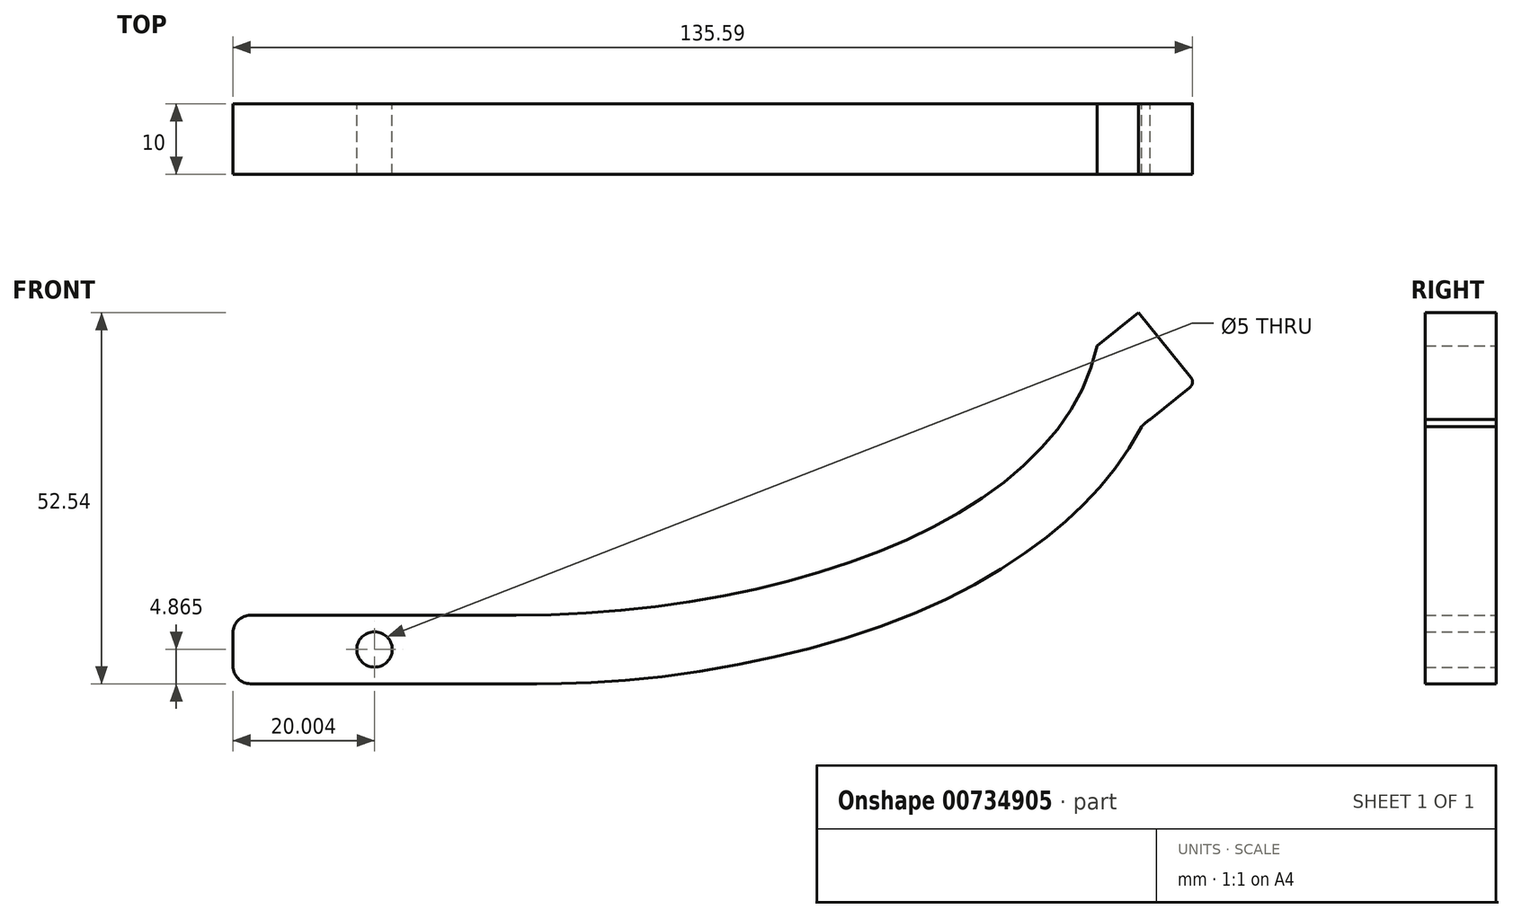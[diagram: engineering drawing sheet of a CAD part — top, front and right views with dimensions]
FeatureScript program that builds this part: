
annotation { "Feature Type Name" : "Feature", "Feature Type Description" : "" }
export const myFeature = defineFeature(function(context is Context, id is Id, definition is map)
    precondition{}
    {
        {
            var Q0;
            Q0=qCreatedBy(makeId("Front.planeOp"),FACE);
            var sketch = newSketch(context, id + "F0", { "sketchPlane" : qUnion([Q0])});
            skPoint(sketch, "E0", {"position": v(36.8, 57.3) * mm});
            skPoint(sketch, "E1", {"position": v(-45.29, 19.17) * mm});
            skPoint(sketch, "E2", {"position": v(-85.29, 19.17) * mm});
            skPoint(sketch, "E3", {"position": v(-65.29, 19.17) * mm});
            skLineSegment(sketch, "E4", {"start": v(-82.79, 19.17) * mm, "end": v(-65.29, 19.17) * mm});
            skLineSegment(sketch, "E5", {"start": v(-45.29, 19.17) * mm, "end": v(-65.29, 19.17) * mm});
            skFitSpline(sketch, "E6", {"points": [v(-45.29, 19.17) * mm, v(36.8, 57.3) * mm], "startDerivative": vector(113.65, 0) * mm, "endDerivative": vector(15.59, 73.8) * mm});
            skLineSegment(sketch, "E7.0", {"start": v(43.68, 47.42) * mm, "end": v(44.3, 46.86) * mm});
            skFitSpline(sketch, "E7.1", {"points": [v(-45.29, 9.47) * mm, v(-40.26, 9.47) * mm, v(-30.19, 9.92) * mm, v(-15.36, 11.91) * mm, v(-1.17, 15.2) * mm, v(12.04, 19.85) * mm, v(21.96, 24.9) * mm, v(29.05, 29.76) * mm, v(33.89, 33.84) * mm, v(38.17, 38.41) * mm, v(41.79, 43.5) * mm, v(44.6, 49.13) * mm, v(45.85, 53.2) * mm, v(46.3, 55.29) * mm]});
            skLineSegment(sketch, "E7.2", {"start": v(-45.29, 9.47) * mm, "end": v(-65.29, 9.47) * mm});
            skLineSegment(sketch, "E7.3", {"start": v(-82.79, 9.47) * mm, "end": v(-65.29, 9.47) * mm});
            skLineSegment(sketch, "E8", {"start": v(-85.29, 11.97) * mm, "end": v(-85.29, 16.67) * mm});
            skLineSegment(sketch, "E9", {"start": v(-45.29, 19.17) * mm, "end": v(-45.29, 9.47) * mm});
            skLineSegment(sketch, "E10", {"start": v(36.8, 57.3) * mm, "end": v(42.65, 62) * mm});
            skLineSegment(sketch, "E11", {"start": v(42.65, 62) * mm, "end": v(50.07, 52.78) * mm});
            skLineSegment(sketch, "E12", {"start": v(49.92, 51.37) * mm, "end": v(44.3, 46.86) * mm});
            skPoint(sketch, "E13", {"position": v(39.73, 59.65) * mm});
            skPoint(sketch, "E14", {"position": v(47.5, 49.43) * mm});
            skLineSegment(sketch, "E15", {"start": v(-65.29, 9.47) * mm, "end": v(-65.29, 19.17) * mm});
            skPoint(sketch, "E16", {"position": v(-65.29, 14.32) * mm});
            skCircle(sketch, "E17", {"center": v(-65.29, 14.32) * mm, "radius": 2.5 * mm});
            skArc(sketch, "E18.filletArc", {"start": v(-82.79, 19.17) * mm, "mid": v(-84.55, 18.44) * mm, "end": v(-85.29, 16.67) * mm});
            skPoint(sketch, "E19.visualSharp", {"position": v(-85.29, 9.47) * mm});
            skArc(sketch, "E19.filletArc", {"start": v(-85.29, 11.97) * mm, "mid": v(-84.55, 10.2) * mm, "end": v(-82.79, 9.47) * mm});
            skPoint(sketch, "E20.visualSharp", {"position": v(50.7, 52) * mm});
            skArc(sketch, "E20.filletArc", {"start": v(49.92, 51.37) * mm, "mid": v(50.29, 52.05) * mm, "end": v(50.07, 52.78) * mm});
            skPoint(sketch, "E21", {"position": v(42.92, 45.87) * mm});
            skFitSpline(sketch, "E22", {"points": [v(42.58, 45.22) * mm, v(44.3, 46.86) * mm], "startDerivative": vector(1.08, 0.77) * mm, "endDerivative": vector(4.05, 2.72) * mm});
            skSolve(sketch);
        }
        {
            var Q0;
            Q0 = qSketchRegion(id + "F0", true);
            extrude(context, id + "F1", {"entities" : qUnion([Q0]), "depth" : 10 * mm, "offsetDistance" : 25 * mm});
        }
    });
